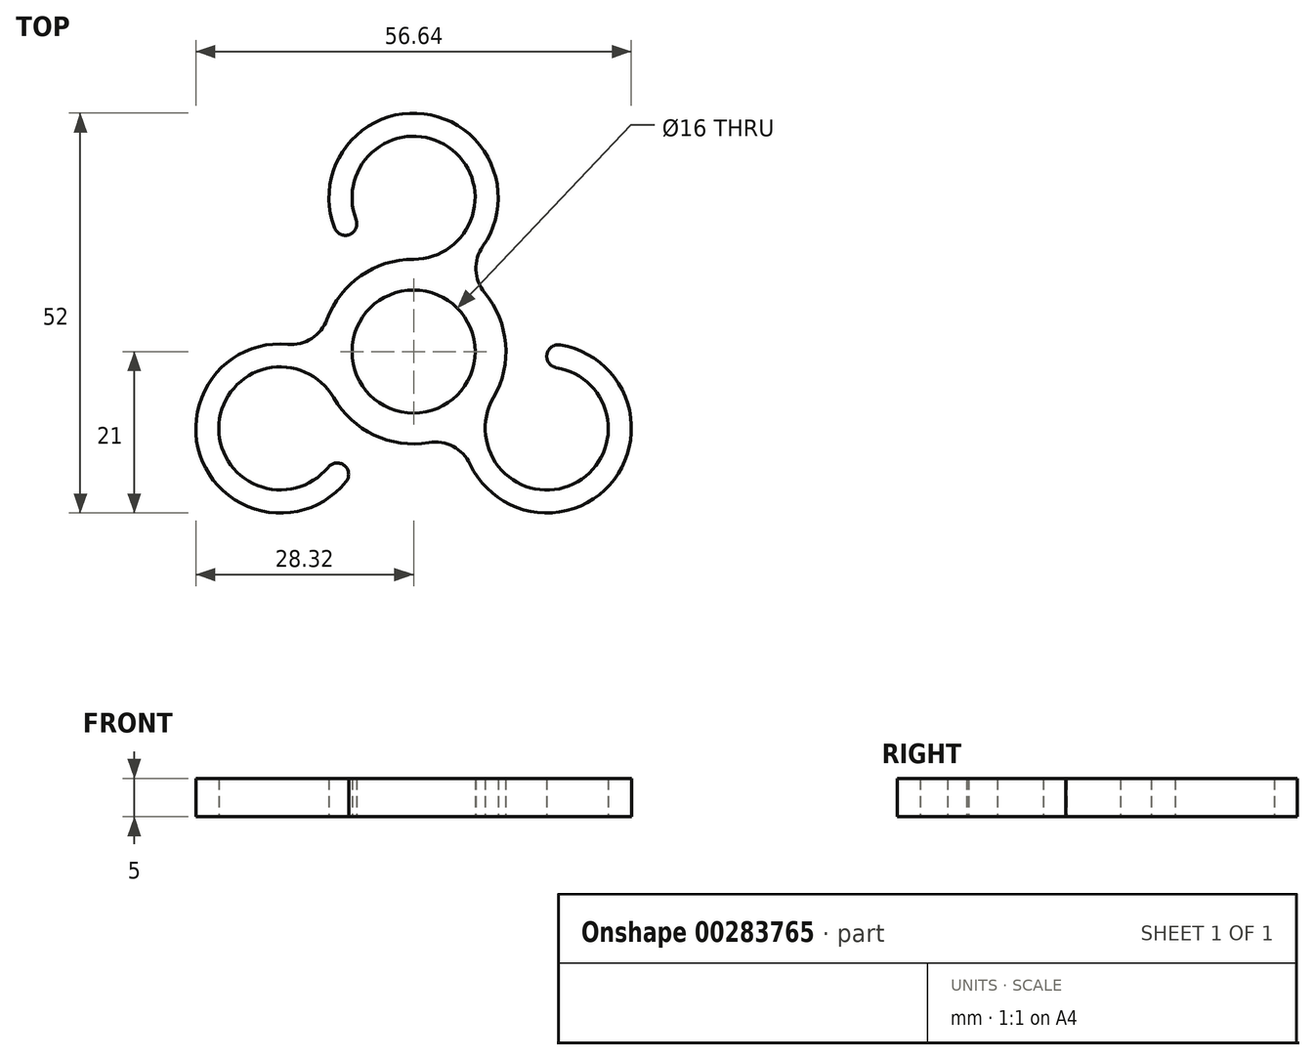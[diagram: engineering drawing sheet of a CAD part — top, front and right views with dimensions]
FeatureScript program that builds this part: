
annotation { "Feature Type Name" : "Feature", "Feature Type Description" : "" }
export const myFeature = defineFeature(function(context is Context, id is Id, definition is map)
    precondition{}
    {
        {
            var Q0;
            Q0=qCreatedBy(makeId("Top.planeOp"),FACE);
            var sketch = newSketch(context, id + "F0", { "sketchPlane" : qUnion([Q0])});
            skCircle(sketch, "E0", {"center": v(0, 0) * mm, "radius": 8 * mm});
            skArc(sketch, "E1", {"start": v(0, 12) * mm, "mid": v(-6.84, 9.86) * mm, "end": v(-11.24, 4.2) * mm});
            skArc(sketch, "E2", {"start": v(0, 12) * mm, "mid": v(4.54, 26.59) * mm, "end": v(-7.47, 17.14) * mm});
            skArc(sketch, "E3", {"start": v(9.01, 13.7) * mm, "mid": v(1.35, 30.92) * mm, "end": v(-10.28, 16.07) * mm});
            skLineSegment(sketch, "E4", {"start": v(-8.12, 15.3) * mm, "end": v(-8.12, 15.3) * mm});
            skPoint(sketch, "E5.visualSharp", {"position": v(5.67, 10.57) * mm});
            skArc(sketch, "E5.filletArc", {"start": v(9.01, 13.7) * mm, "mid": v(8.11, 10.63) * mm, "end": v(9.25, 7.64) * mm});
            skPoint(sketch, "E6.visualSharp", {"position": v(-6.93, 16) * mm});
            skArc(sketch, "E6.filletArc", {"start": v(-8.12, 15.3) * mm, "mid": v(-7.46, 16.1) * mm, "end": v(-7.47, 17.14) * mm});
            skPoint(sketch, "E7.visualSharp", {"position": v(-9.53, 14.5) * mm});
            skArc(sketch, "E7.filletArc", {"start": v(-10.28, 16.07) * mm, "mid": v(-9.38, 15.2) * mm, "end": v(-8.12, 15.3) * mm});
            skArc(sketch, "E8.1.0", {"start": v(-16.36, 0.96) * mm, "mid": v(-13.26, 1.71) * mm, "end": v(-11.24, 4.2) * mm});
            skPoint(sketch, "E8.1.1", {"position": v(-10.4, -14) * mm});
            skPoint(sketch, "E8.1.2", {"position": v(-12, -0.38) * mm});
            skArc(sketch, "E8.1.3", {"start": v(-16.36, 0.96) * mm, "mid": v(-27.45, -14.3) * mm, "end": v(-8.78, -16.94) * mm});
            skArc(sketch, "E8.1.4", {"start": v(-10.4, -6) * mm, "mid": v(-25.3, -9.37) * mm, "end": v(-11.11, -15.04) * mm});
            skPoint(sketch, "E8.1.5", {"position": v(-7.8, -15.5) * mm});
            skArc(sketch, "E8.1.6", {"start": v(-8.78, -16.94) * mm, "mid": v(-8.47, -15.72) * mm, "end": v(-9.2, -14.7) * mm});
            skArc(sketch, "E8.1.7", {"start": v(-9.2, -14.7) * mm, "mid": v(-10.22, -14.51) * mm, "end": v(-11.11, -15.04) * mm});
            skArc(sketch, "E8.2.0", {"start": v(7.35, -14.65) * mm, "mid": v(5.15, -12.34) * mm, "end": v(2, -11.83) * mm});
            skPoint(sketch, "E8.2.1", {"position": v(17.32, -2) * mm});
            skPoint(sketch, "E8.2.2", {"position": v(6.32, -10.2) * mm});
            skArc(sketch, "E8.2.3", {"start": v(7.35, -14.65) * mm, "mid": v(26.1, -16.63) * mm, "end": v(19.06, 0.86) * mm});
            skArc(sketch, "E8.2.4", {"start": v(10.4, -6) * mm, "mid": v(20.76, -17.22) * mm, "end": v(18.58, -2.1) * mm});
            skPoint(sketch, "E8.2.5", {"position": v(17.32, 1) * mm});
            skArc(sketch, "E8.2.6", {"start": v(19.06, 0.86) * mm, "mid": v(17.85, 0.52) * mm, "end": v(17.32, -0.62) * mm});
            skArc(sketch, "E8.2.7", {"start": v(17.32, -0.62) * mm, "mid": v(17.68, -1.6) * mm, "end": v(18.58, -2.1) * mm});
            skArc(sketch, "E9.trimOffspring", {"start": v(10.4, -6) * mm, "mid": v(11.96, 1) * mm, "end": v(9.25, 7.64) * mm});
            skArc(sketch, "E10.trimOffspring", {"start": v(-10.4, -6) * mm, "mid": v(-5.11, -10.86) * mm, "end": v(2, -11.83) * mm});
            skSolve(sketch);
        }
        {
            var Q0;
            Q0=makeQuery(id+"F0.imprint","IMPRINT",FACE,{"disambiguationData":[TD([[makeQuery(id+"F0.imprint","IMPRINT",EDGE,{"derivedFrom":sQuery(id+"F0.wireOp",EDGE,"E0")}),-1.0]])]});
            extrude(context, id + "F1", {"entities" : qUnion([Q0]), "depth" : 5 * mm});
        }
    });
